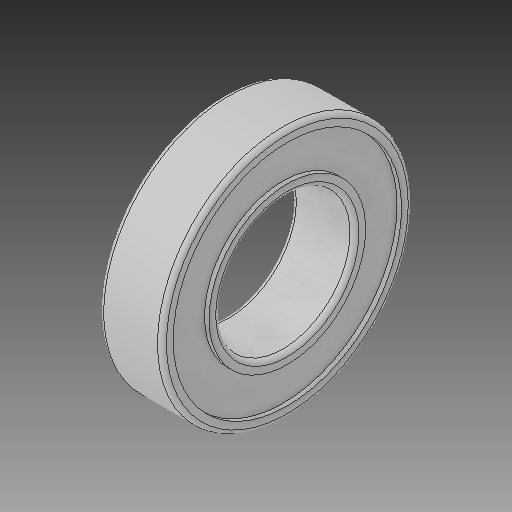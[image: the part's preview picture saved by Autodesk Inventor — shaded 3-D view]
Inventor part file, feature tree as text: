
AUTODESK INVENTOR PART (.ipt)
format: ipt  version: 2017 (Build 210142000, 142)  size: 180,736 bytes
history: native  units: in
note: dims shown in document units (in); Inventor stores cm internally (conversion verified against a paired STEP export)
features: fillet x1
ambient origin geometry x8: Origin, YZ Plane, XZ Plane, XY Plane, X Axis, Y Axis, Z Axis, Center Point
bodies: Solid1 (feature_tree)
feature tree (1):
  fillet  "Fillet1"  [1 undecoded]
note: 1 required parameter value undecoded (feature->parameter linkage not recoverable at this tier; creation-order binding heuristic only, values carry confidence <= 0.55)
